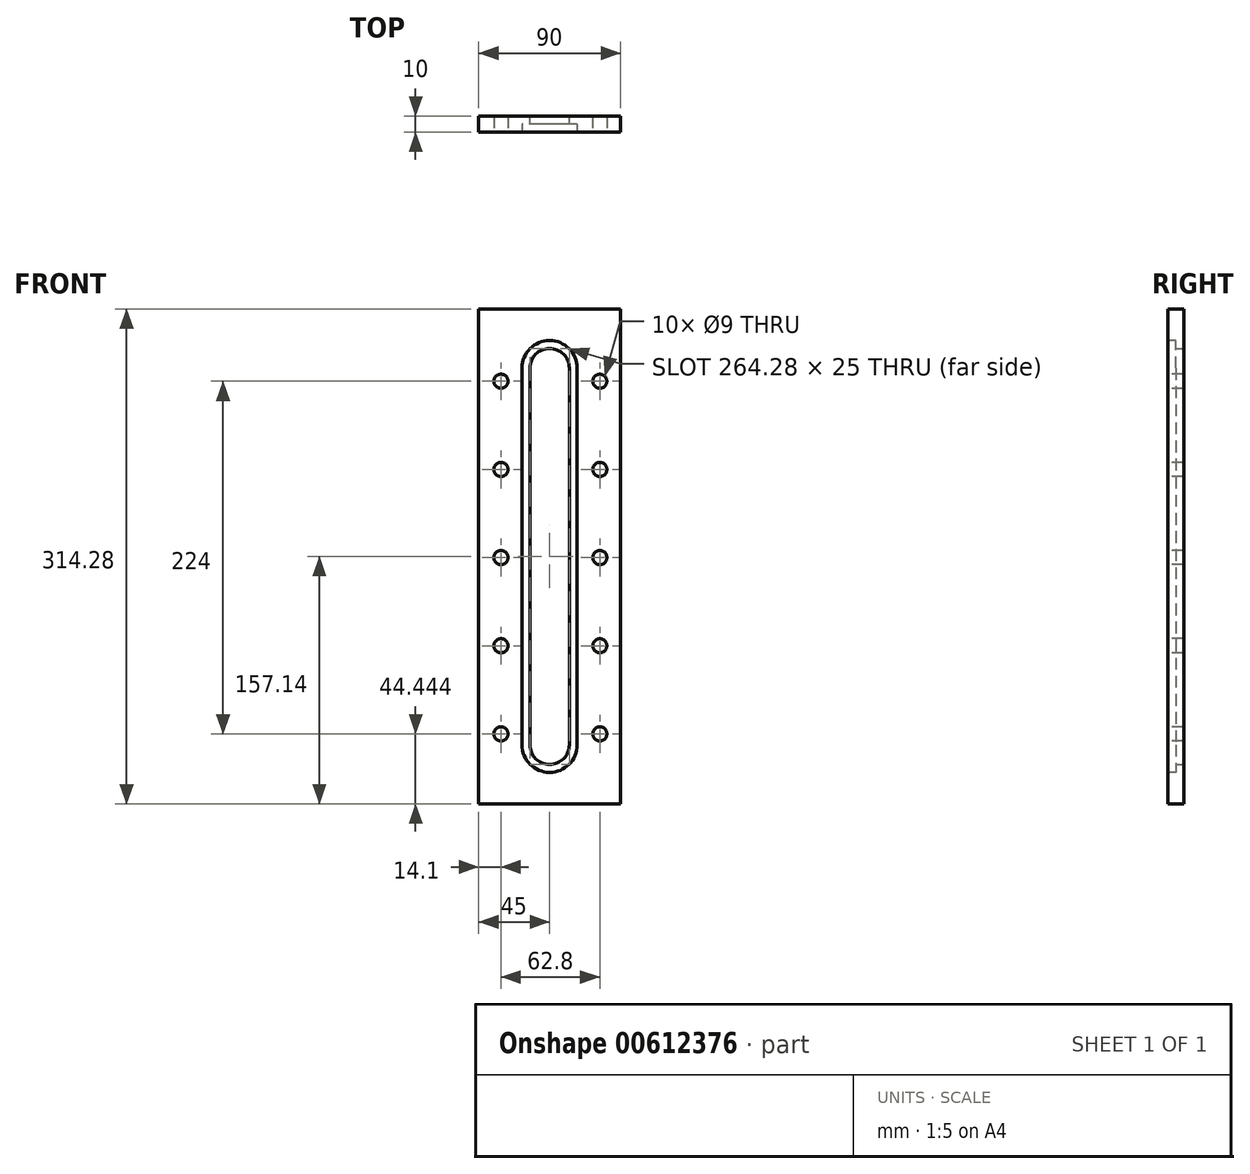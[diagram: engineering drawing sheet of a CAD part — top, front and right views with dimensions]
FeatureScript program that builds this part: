
annotation { "Feature Type Name" : "Feature", "Feature Type Description" : "" }
export const myFeature = defineFeature(function(context is Context, id is Id, definition is map)
    precondition{}
    {
        {
            var Q0;
            Q0=qCreatedBy(makeId("Front.planeOp"),FACE);
            var sketch = newSketch(context, id + "F0", { "sketchPlane" : qUnion([Q0])});
            skLineSegment(sketch, "E0.bottom", {"start": v(-45, 157.14) * mm, "end": v(45, 157.14) * mm});
            skLineSegment(sketch, "E0.top", {"start": v(-45, -157.14) * mm, "end": v(45, -157.14) * mm});
            skLineSegment(sketch, "E0.left", {"start": v(-45, 157.14) * mm, "end": v(-45, -157.14) * mm});
            skLineSegment(sketch, "E0.right", {"start": v(45, 157.14) * mm, "end": v(45, -157.14) * mm});
            skLineSegment(sketch, "E1.left", {"start": v(-12.5, 119.64) * mm, "end": v(-12.5, -119.64) * mm});
            skLineSegment(sketch, "E1.right", {"start": v(12.5, 119.64) * mm, "end": v(12.5, -119.64) * mm});
            skArc(sketch, "E2", {"start": v(12.5, 119.64) * mm, "mid": v(0, 132.14) * mm, "end": v(-12.5, 119.64) * mm});
            skArc(sketch, "E3", {"start": v(-12.5, -119.64) * mm, "mid": v(0, -132.14) * mm, "end": v(12.5, -119.64) * mm});
            skSolve(sketch);
        }
        {
            var Q0;
            Q0 = qSketchRegion(id + "F0", true);
            extrude(context, id + "F1", {"entities" : qUnion([Q0]), "depth" : 10 * mm, "offsetDistance" : 25 * mm});
        }
        {
            var Q0;
            Q0=makeQuery(id+"F1.opExtrude","CAP_FACE",FACE,{"disambiguationData":[OSD([sQuery(id+"F0.wireOp",EDGE,"E0.bottom"),sQuery(id+"F0.wireOp",EDGE,"E0.top"),sQuery(id+"F0.wireOp",EDGE,"E0.left"),sQuery(id+"F0.wireOp",EDGE,"E0.right"),sQuery(id+"F0.wireOp",EDGE,"E1.left"),sQuery(id+"F0.wireOp",EDGE,"E1.right"),sQuery(id+"F0.wireOp",EDGE,"E2"),sQuery(id+"F0.wireOp",EDGE,"E3")])],"isStart":false});
            var sketch = newSketch(context, id + "F2", { "sketchPlane" : qUnion([Q0])});
            skArc(sketch, "E4.0", {"start": v(17.5, 119.64) * mm, "mid": v(0, 137.14) * mm, "end": v(-17.5, 119.64) * mm});
            skLineSegment(sketch, "E4.1", {"start": v(17.5, 119.64) * mm, "end": v(17.5, -119.64) * mm});
            skArc(sketch, "E4.2", {"start": v(-17.5, -119.64) * mm, "mid": v(0, -137.14) * mm, "end": v(17.5, -119.64) * mm});
            skLineSegment(sketch, "E4.3", {"start": v(-17.5, 119.64) * mm, "end": v(-17.5, -119.64) * mm});
            skSolve(sketch);
        }
        {
            var Q0;
            Q0 = qSketchRegion(id + "F2", true);
            extrude(context, id + "F3", {"entities" : qUnion([Q0]), "operationType" : NewBodyOperationType.REMOVE, "oppositeDirection" : true, "depth" : 5 * mm, "offsetDistance" : 25 * mm});
        }
        {
            var Q0;
            Q0=makeQuery(id+"F1.opExtrude","CAP_FACE",FACE,{"disambiguationData":[OSD([sQuery(id+"F0.wireOp",EDGE,"E0.bottom"),sQuery(id+"F0.wireOp",EDGE,"E0.top"),sQuery(id+"F0.wireOp",EDGE,"E0.left"),sQuery(id+"F0.wireOp",EDGE,"E0.right"),sQuery(id+"F0.wireOp",EDGE,"E1.left"),sQuery(id+"F0.wireOp",EDGE,"E1.right"),sQuery(id+"F0.wireOp",EDGE,"E2"),sQuery(id+"F0.wireOp",EDGE,"E3")])],"isStart":false});
            var sketch = newSketch(context, id + "F4", { "sketchPlane" : qUnion([Q0])});
            skCircle(sketch, "E5", {"center": v(31.9, -112.7) * mm, "radius": 4.5 * mm});
            skCircle(sketch, "E6.3.0", {"center": v(-30.9, -112.7) * mm, "radius": 4.5 * mm});
            skCircle(sketch, "E7", {"center": v(31.9, -56.7) * mm, "radius": 4.5 * mm});
            skCircle(sketch, "E8", {"center": v(31.9, -0.7) * mm, "radius": 4.5 * mm});
            skCircle(sketch, "E9", {"center": v(31.9, 55.3) * mm, "radius": 4.5 * mm});
            skCircle(sketch, "E10", {"center": v(31.9, 111.3) * mm, "radius": 4.5 * mm});
            skCircle(sketch, "E11.MirrorC", {"center": v(-30.9, 111.3) * mm, "radius": 4.5 * mm});
            skCircle(sketch, "E12.MirrorC", {"center": v(-30.9, 55.3) * mm, "radius": 4.5 * mm});
            skCircle(sketch, "E13.MirrorC", {"center": v(-30.9, -0.7) * mm, "radius": 4.5 * mm});
            skCircle(sketch, "E14.MirrorC", {"center": v(-30.9, -56.7) * mm, "radius": 4.5 * mm});
            skSolve(sketch);
        }
        {
            var Q0;
            Q0 = qSketchRegion(id + "F4", true);
            extrude(context, id + "F5", {"entities" : qUnion([Q0]), "operationType" : NewBodyOperationType.REMOVE, "oppositeDirection" : true, "depth" : 25 * mm, "offsetDistance" : 25 * mm});
        }
    });
